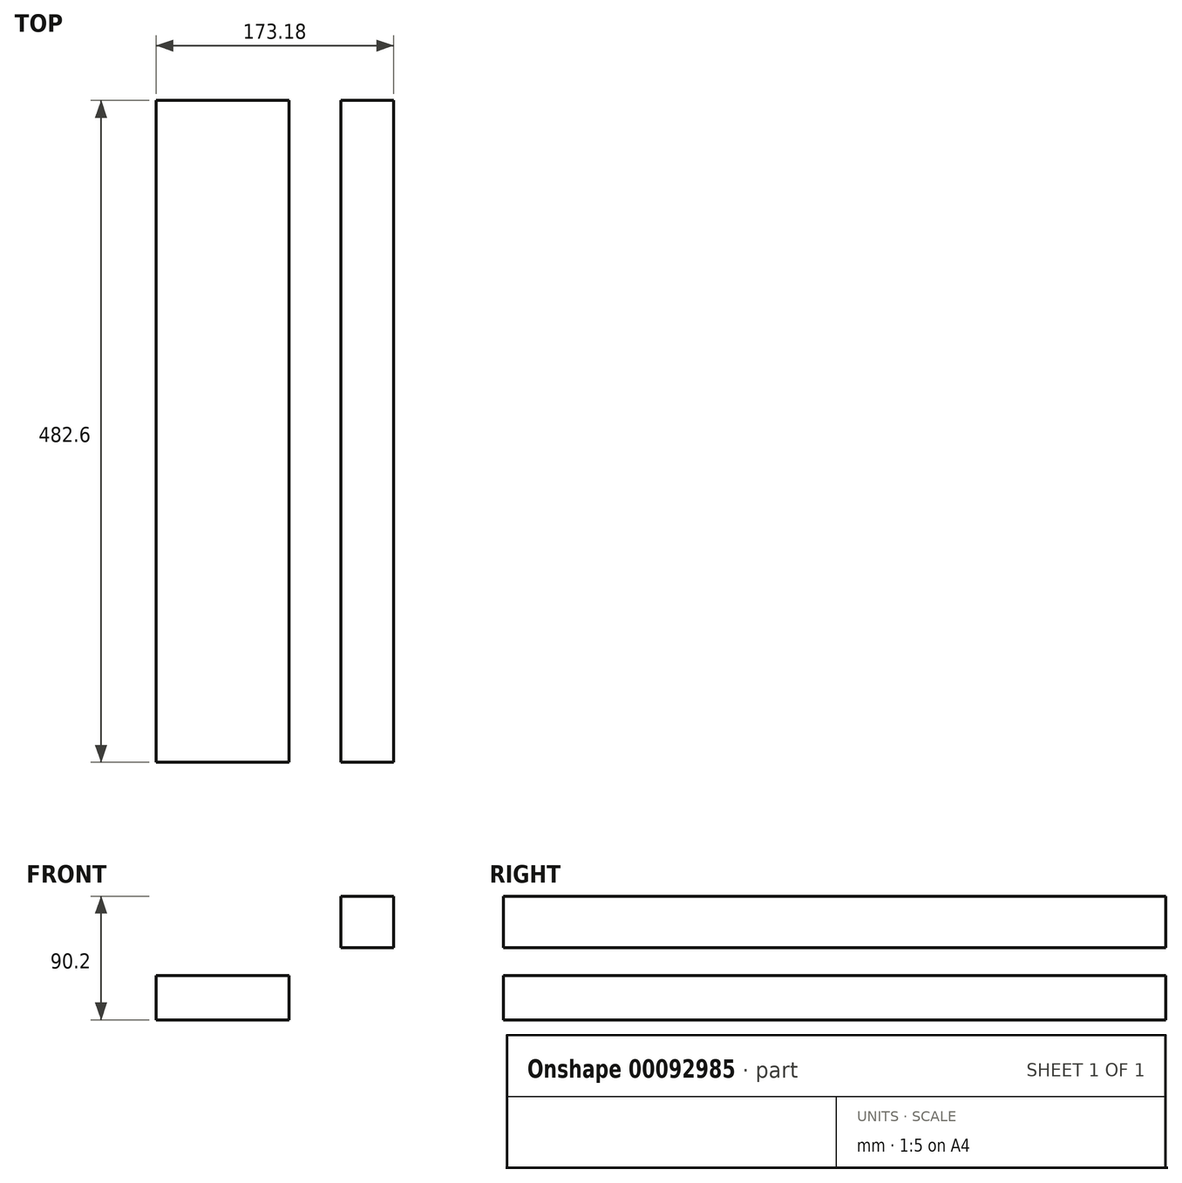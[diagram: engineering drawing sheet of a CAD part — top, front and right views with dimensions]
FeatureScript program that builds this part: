
annotation { "Feature Type Name" : "Feature", "Feature Type Description" : "" }
export const myFeature = defineFeature(function(context is Context, id is Id, definition is map)
    precondition{}
    {
        {
            var Q0;
            Q0=qCreatedBy(makeId("Front.planeOp"),FACE);
            var sketch = newSketch(context, id + "F0", { "sketchPlane" : qUnion([Q0])});
            skLineSegment(sketch, "E0.bottom", {"start": v(48.56, 16.12) * mm, "end": v(-48.56, 16.12) * mm});
            skLineSegment(sketch, "E0.top", {"start": v(48.56, -16.12) * mm, "end": v(-48.56, -16.12) * mm});
            skLineSegment(sketch, "E0.left", {"start": v(48.56, 16.12) * mm, "end": v(48.56, -16.12) * mm});
            skLineSegment(sketch, "E0.right", {"start": v(-48.56, 16.12) * mm, "end": v(-48.56, -16.12) * mm});
            skPoint(sketch, "E0.middle", {"position": v(0, 0) * mm});
            skLineSegment(sketch, "E1.bottom", {"start": v(124.62, 74.08) * mm, "end": v(86.2, 74.08) * mm});
            skLineSegment(sketch, "E1.top", {"start": v(124.62, 36.3) * mm, "end": v(86.2, 36.3) * mm});
            skLineSegment(sketch, "E1.left", {"start": v(124.62, 74.08) * mm, "end": v(124.62, 36.3) * mm});
            skLineSegment(sketch, "E1.right", {"start": v(86.2, 74.08) * mm, "end": v(86.2, 36.3) * mm});
            skPoint(sketch, "E1.middle", {"position": v(105.41, 55.2) * mm});
            skLineSegment(sketch, "E2", {"start": v(48.56, 16.12) * mm, "end": v(48.56, 42.6) * mm});
            skArc(sketch, "E3", {"start": v(48.56, 42.6) * mm, "mid": v(52.25, 51.5) * mm, "end": v(61.16, 55.2) * mm});
            skLineSegment(sketch, "E4", {"start": v(61.16, 55.2) * mm, "end": v(105.41, 55.2) * mm});
            skSolve(sketch);
        }
        {
            var Q0;
            Q0=makeQuery(id+"F0.imprint","IMPRINT",FACE,{"disambiguationData":[TD([[makeQuery(id+"F0.imprint","IMPRINT",EDGE,{"derivedFrom":sQuery(id+"F0.wireOp",EDGE,"E0.bottom")}),1.0]])]});
            var Q1;
            {var subQ0=sQuery(id+"F0.wireOp",EDGE,"E1.bottom");Q1=makeQuery(id+"F0.imprint","IMPRINT",FACE,{"disambiguationData":[TD([[makeQuery(id+"F0.imprint","IMPRINT",EDGE,{"derivedFrom":subQ0}),1.0]])]});}
            extrude(context, id + "F1", {"entities" : qUnion([Q0, Q1]), "endBound" : BoundingType.SYMMETRIC, "depth" : 482.6 * mm});
        }
        {
            var Q0;
            Q0=sQuery(id+"F0.wireOp",EDGE,"E2");
            var Q1;
            Q1=sQuery(id+"F0.wireOp",EDGE,"E3");
            var Q2;
            Q2=sQuery(id+"F0.wireOp",EDGE,"E4");
            extrude(context, id + "F2", {"bodyType" : ToolBodyType.SURFACE, "surfaceEntities" : qUnion([Q0, Q1, Q2]), "depth" : 482.6 * mm});
        }
    });
